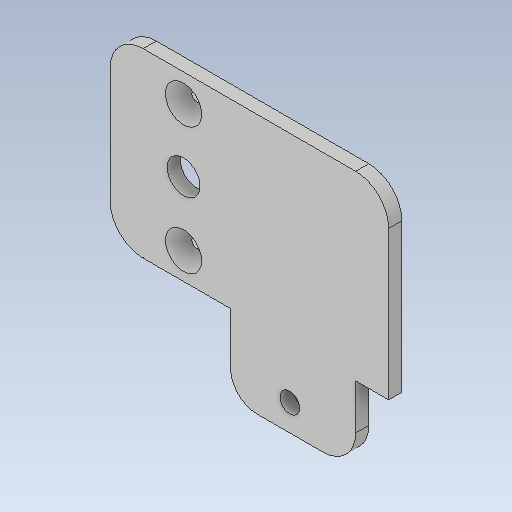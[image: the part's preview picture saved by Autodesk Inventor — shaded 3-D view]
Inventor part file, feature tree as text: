
AUTODESK INVENTOR PART (.ipt)
format: ipt  version: 2020 (Build 240168000, 168)  size: 123,904 bytes
history: native  units: mm
features: other x1, extrude x1, chamfer x1, sketch x1
ambient origin geometry x8: Origin, YZ Plane, XZ Plane, XY Plane, X Axis, Y Axis, Z Axis, Center Point
bodies: Body1 (feature_tree)
feature tree (4):
  other  "Твердое тело1"
  extrude  "Выдавливание1"  Depth=5.0mm
  chamfer  "Фаска5"  Distance=2.0mm
  sketch  "Эскиз1"
